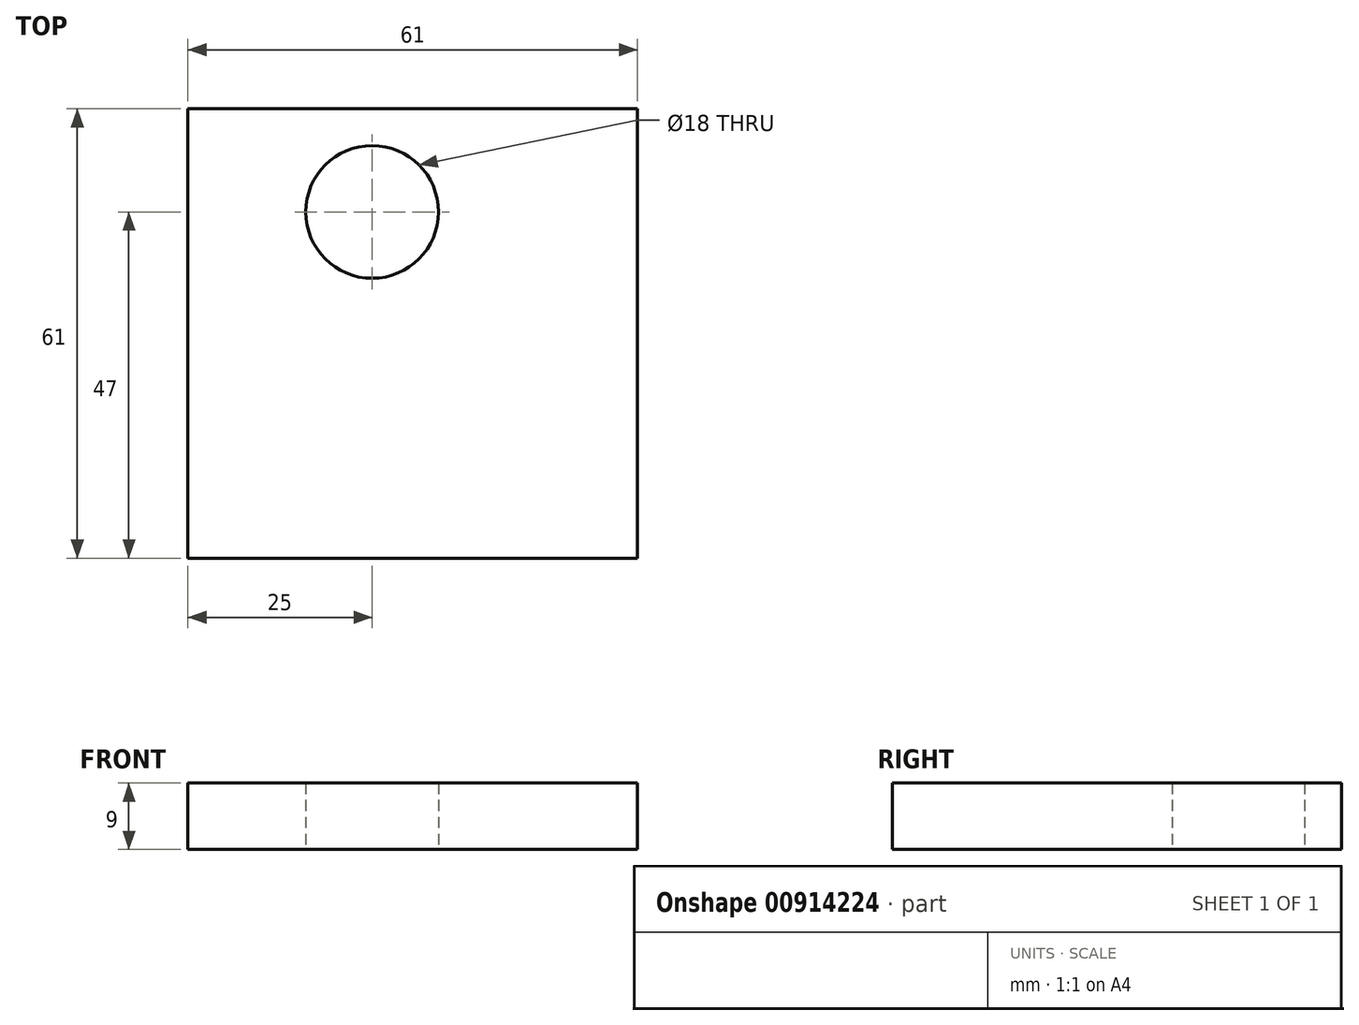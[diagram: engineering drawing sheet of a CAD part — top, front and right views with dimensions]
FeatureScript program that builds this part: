
annotation { "Feature Type Name" : "Feature", "Feature Type Description" : "" }
export const myFeature = defineFeature(function(context is Context, id is Id, definition is map)
    precondition{}
    {
        {
            var Q0;
            Q0=qCreatedBy(makeId("Top.planeOp"),FACE);
            var sketch = newSketch(context, id + "F0", { "sketchPlane" : qUnion([Q0])});
            skLineSegment(sketch, "E0.bottom", {"start": v(30.5, 30.5) * mm, "end": v(-30.5, 30.5) * mm});
            skLineSegment(sketch, "E0.top", {"start": v(30.5, -30.5) * mm, "end": v(-30.5, -30.5) * mm});
            skLineSegment(sketch, "E0.left", {"start": v(30.5, 30.5) * mm, "end": v(30.5, -30.5) * mm});
            skLineSegment(sketch, "E0.right", {"start": v(-30.5, 30.5) * mm, "end": v(-30.5, -30.5) * mm});
            skPoint(sketch, "E0.middle", {"position": v(0, 0) * mm});
            skPoint(sketch, "E1", {"position": v(-5.5, 16.5) * mm});
            skCircle(sketch, "E2", {"center": v(-5.5, 16.5) * mm, "radius": 9 * mm});
            skSolve(sketch);
        }
        {
            var Q0;
            Q0 = qSketchRegion(id + "F0", true);
            extrude(context, id + "F1", {"entities" : qUnion([Q0]), "depth" : 9 * mm, "offsetDistance" : 25 * mm});
        }
    });
